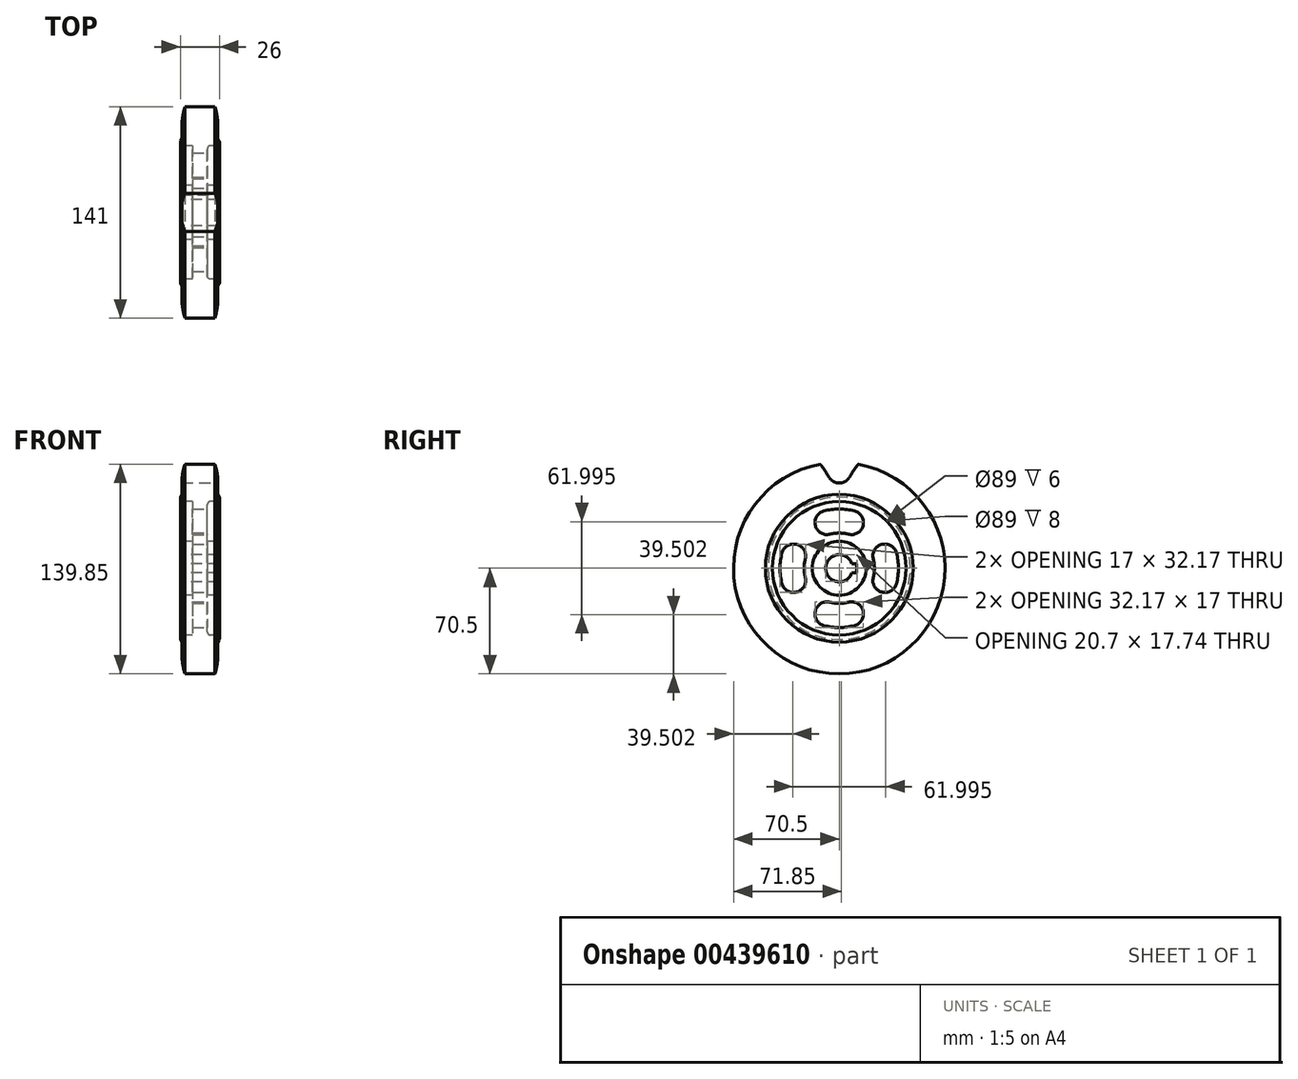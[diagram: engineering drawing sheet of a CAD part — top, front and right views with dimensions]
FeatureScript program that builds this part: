
annotation { "Feature Type Name" : "Feature", "Feature Type Description" : "" }
export const myFeature = defineFeature(function(context is Context, id is Id, definition is map)
    precondition{}
    {
        {
            var Q0;
            Q0=qCreatedBy(makeId("Front.planeOp"),FACE);
            var sketch = newSketch(context, id + "F0", { "sketchPlane" : qUnion([Q0])});
            skLineSegment(sketch, "E0", {"start": v(-89.89, 0) * mm, "end": v(89.89, 0) * mm, "construction": true});
            skLineSegment(sketch, "E1", {"start": v(0, -64.7) * mm, "end": v(0, 108.64) * mm, "construction": true});
            skLineSegment(sketch, "E2", {"start": v(0, 9) * mm, "end": v(-13, 9) * mm});
            skLineSegment(sketch, "E3", {"start": v(-13, 9) * mm, "end": v(-13, 44.5) * mm});
            skLineSegment(sketch, "E4", {"start": v(-13, 44.5) * mm, "end": v(-13, 47.5) * mm});
            skArc(sketch, "E5", {"start": v(-12, 57.23) * mm, "mid": v(-11.5, 63.94) * mm, "end": v(-10, 70.5) * mm});
            skLineSegment(sketch, "E6", {"start": v(-10, 70.5) * mm, "end": v(0, 70.5) * mm});
            skLineSegment(sketch, "E7.MirrorCS", {"start": v(13, 44.5) * mm, "end": v(13, 47.5) * mm});
            skLineSegment(sketch, "E8.MirrorCS", {"start": v(13, 9) * mm, "end": v(13, 44.5) * mm});
            skLineSegment(sketch, "E9.MirrorCS", {"start": v(0, 9) * mm, "end": v(13, 9) * mm});
            skLineSegment(sketch, "E10.bottom", {"start": v(-16.55, 44.5) * mm, "end": v(-5, 44.5) * mm});
            skLineSegment(sketch, "E10.top", {"start": v(-16.55, 18) * mm, "end": v(-5, 18) * mm});
            skLineSegment(sketch, "E10.left", {"start": v(-16.55, 44.5) * mm, "end": v(-16.55, 18) * mm});
            skLineSegment(sketch, "E10.right", {"start": v(-5, 44.5) * mm, "end": v(-5, 18) * mm});
            skLineSegment(sketch, "E11.MirrorCS", {"start": v(5, 44.5) * mm, "end": v(5, 18) * mm});
            skLineSegment(sketch, "E12.MirrorCS", {"start": v(16.55, 44.5) * mm, "end": v(5, 44.5) * mm});
            skLineSegment(sketch, "E13.MirrorCS", {"start": v(16.55, 18) * mm, "end": v(5, 18) * mm});
            skLineSegment(sketch, "E14.MirrorCS", {"start": v(16.55, 44.5) * mm, "end": v(16.55, 18) * mm});
            skLineSegment(sketch, "E15", {"start": v(-13, 47.5) * mm, "end": v(-12, 49.25) * mm});
            skLineSegment(sketch, "E16", {"start": v(-12, 49.25) * mm, "end": v(-12, 57.23) * mm});
            skArc(sketch, "E17.MirrorCS", {"start": v(12, 57.23) * mm, "mid": v(11.5, 63.94) * mm, "end": v(10, 70.5) * mm});
            skLineSegment(sketch, "E18.MirrorCS", {"start": v(12, 49.25) * mm, "end": v(12, 57.23) * mm});
            skLineSegment(sketch, "E19.MirrorCS", {"start": v(13, 47.5) * mm, "end": v(12, 49.25) * mm});
            skLineSegment(sketch, "E20.MirrorCS", {"start": v(0, 205.7) * mm, "end": v(0, 32.36) * mm, "construction": true});
            skLineSegment(sketch, "E21.MirrorCS", {"start": v(10, 70.5) * mm, "end": v(0, 70.5) * mm});
            skSolve(sketch);
        }
        {
            var Q0;
            {var subQ1=sQuery(id+"F0.wireOp",EDGE,"E2");Q0=makeQuery(id+"F0.imprint","IMPRINT",FACE,{"disambiguationData":[TD([[makeQuery(id+"F0.imprint","IMPRINT",EDGE,{"derivedFrom":subQ1}),-1.0]])]});}
            var Q1;
            Q1=sQuery(id+"F0.wireOp",EDGE,"E0");
            revolve(context, id + "F1", {"entities" : qUnion([Q0]), "axis" : qUnion([Q1]), "revolveType" : RevolveType.FULL});
        }
        {
            var Q0;
            Q0=qCreatedBy(makeId("Right.planeOp"),FACE);
            var sketch = newSketch(context, id + "F2", { "sketchPlane" : qUnion([Q0])});
            skLineSegment(sketch, "E22", {"start": v(0, 74.56) * mm, "end": v(0, -73.36) * mm, "construction": true});
            skCircle(sketch, "E23", {"center": v(0, 0) * mm, "radius": 64.75 * mm, "construction": true});
            skLineSegment(sketch, "E24", {"start": v(0, 64.75) * mm, "end": v(84.25, 16.1) * mm, "construction": true});
            skLineSegment(sketch, "E25", {"start": v(0, 64.75) * mm, "end": v(-84.25, 16.1) * mm, "construction": true});
            skArc(sketch, "E26", {"start": v(-6.87, 60.78) * mm, "mid": v(0, 56.81) * mm, "end": v(6.87, 60.78) * mm});
            skArc(sketch, "E27", {"start": v(11.86, 68.34) * mm, "mid": v(9.25, 64.64) * mm, "end": v(6.87, 60.78) * mm});
            skArc(sketch, "E28", {"start": v(11.86, 68.34) * mm, "mid": v(12.27, 68.86) * mm, "end": v(12.7, 69.35) * mm});
            skArc(sketch, "E29.MirrorCS", {"start": v(-11.86, 68.34) * mm, "mid": v(-12.27, 68.86) * mm, "end": v(-12.7, 69.35) * mm});
            skArc(sketch, "E30.MirrorCS", {"start": v(-11.86, 68.34) * mm, "mid": v(-9.25, 64.64) * mm, "end": v(-6.87, 60.78) * mm});
            skPoint(sketch, "E31.orphan", {"position": v(21.73, 73.23) * mm});
            skPoint(sketch, "E32.orphan", {"position": v(-21.73, 73.23) * mm});
            skArc(sketch, "E33.trimOffspring", {"start": v(12.7, 69.35) * mm, "mid": v(0, 70.5) * mm, "end": v(-12.7, 69.35) * mm});
            skSolve(sketch);
        }
        {
            var Q0;
            Q0=makeQuery(id+"F2.imprint","IMPRINT",FACE,{"disambiguationData":[TD([[makeQuery(id+"F2.imprint","IMPRINT",EDGE,{"derivedFrom":sQuery(id+"F2.wireOp",EDGE,"E26")}),1.0]])]});
            extrude(context, id + "F3", {"entities" : qUnion([Q0]), "operationType" : NewBodyOperationType.REMOVE, "endBound" : BoundingType.THROUGH_ALL, "oppositeDirection" : true, "depth" : 25 * mm, "hasSecondDirection" : true, "secondDirectionBound" : BoundingType.THROUGH_ALL, "secondDirectionOppositeDirection" : false, "secondDirectionDepth" : 25 * mm});
        }
        {
            var Q0;
            Q0=qCreatedBy(makeId("Right.planeOp"),FACE);
            var sketch = newSketch(context, id + "F4", { "sketchPlane" : qUnion([Q0])});
            skLineSegment(sketch, "E34", {"start": v(0, -69.16) * mm, "end": v(0, 68.82) * mm, "construction": true});
            skLineSegment(sketch, "E35", {"start": v(-70.48, 0) * mm, "end": v(76.97, 0) * mm, "construction": true});
            skLineSegment(sketch, "E36.bottom", {"start": v(4.41, 3) * mm, "end": v(11.7, 3) * mm});
            skLineSegment(sketch, "E36.top", {"start": v(4.41, -3) * mm, "end": v(11.7, -3) * mm});
            skLineSegment(sketch, "E36.left", {"start": v(4.41, 3) * mm, "end": v(4.41, -3) * mm});
            skLineSegment(sketch, "E36.right", {"start": v(11.7, 3) * mm, "end": v(11.7, -3) * mm});
            skLineSegment(sketch, "E37", {"start": v(-9, 11.79) * mm, "end": v(-9, -13.84) * mm, "construction": true});
            skCircle(sketch, "E38", {"center": v(0, 0) * mm, "radius": 31.5 * mm, "construction": true});
            skLineSegment(sketch, "E39", {"start": v(0, 0) * mm, "end": v(-40.07, 10.74) * mm, "construction": true});
            skLineSegment(sketch, "E40", {"start": v(0, 0) * mm, "end": v(-40.07, -10.74) * mm, "construction": true});
            skArc(sketch, "E41", {"start": v(-22.7, 6.08) * mm, "mid": v(-28.36, 15.88) * mm, "end": v(-38.15, 10.22) * mm});
            skArc(sketch, "E42", {"start": v(-38.15, -10.22) * mm, "mid": v(-28.36, -15.88) * mm, "end": v(-22.7, -6.08) * mm});
            skArc(sketch, "E43", {"start": v(-38.15, 10.22) * mm, "mid": v(-39.5, 0) * mm, "end": v(-38.15, -10.22) * mm});
            skArc(sketch, "E44", {"start": v(-22.7, 6.08) * mm, "mid": v(-23.5, 0) * mm, "end": v(-22.7, -6.08) * mm});
            skArc(sketch, "E45.1.0", {"start": v(-6.08, -22.7) * mm, "mid": v(-15.88, -28.36) * mm, "end": v(-10.22, -38.15) * mm});
            skArc(sketch, "E45.1.1", {"start": v(-10.22, -38.15) * mm, "mid": v(0, -39.5) * mm, "end": v(10.22, -38.15) * mm});
            skArc(sketch, "E45.1.2", {"start": v(-6.08, -22.7) * mm, "mid": v(0, -23.5) * mm, "end": v(6.08, -22.7) * mm});
            skArc(sketch, "E45.1.3", {"start": v(10.22, -38.15) * mm, "mid": v(15.88, -28.36) * mm, "end": v(6.08, -22.7) * mm});
            skArc(sketch, "E45.2.0", {"start": v(22.7, -6.08) * mm, "mid": v(28.36, -15.88) * mm, "end": v(38.15, -10.22) * mm});
            skArc(sketch, "E45.2.1", {"start": v(38.15, -10.22) * mm, "mid": v(39.5, 0) * mm, "end": v(38.15, 10.22) * mm});
            skArc(sketch, "E45.2.2", {"start": v(22.7, -6.08) * mm, "mid": v(23.5, 0) * mm, "end": v(22.7, 6.08) * mm});
            skArc(sketch, "E45.2.3", {"start": v(38.15, 10.22) * mm, "mid": v(28.36, 15.88) * mm, "end": v(22.7, 6.08) * mm});
            skArc(sketch, "E45.3.0", {"start": v(6.08, 22.7) * mm, "mid": v(15.88, 28.36) * mm, "end": v(10.22, 38.15) * mm});
            skArc(sketch, "E45.3.1", {"start": v(10.22, 38.15) * mm, "mid": v(0, 39.5) * mm, "end": v(-10.22, 38.15) * mm});
            skArc(sketch, "E45.3.2", {"start": v(6.08, 22.7) * mm, "mid": v(0, 23.5) * mm, "end": v(-6.08, 22.7) * mm});
            skArc(sketch, "E45.3.3", {"start": v(-10.22, 38.15) * mm, "mid": v(-15.88, 28.36) * mm, "end": v(-6.08, 22.7) * mm});
            skSolve(sketch);
        }
        {
            var Q0;
            Q0 = qSketchRegion(id + "F4", true);
            extrude(context, id + "F5", {"entities" : qUnion([Q0]), "operationType" : NewBodyOperationType.REMOVE, "endBound" : BoundingType.THROUGH_ALL, "oppositeDirection" : true, "depth" : 50 * mm, "hasSecondDirection" : true, "secondDirectionBound" : BoundingType.THROUGH_ALL, "secondDirectionOppositeDirection" : false, "secondDirectionDepth" : 25 * mm});
        }
        {
            var Q0;
            Q0=makeQuery(id+"F1.opRevolve","SWEPT_EDGE",EDGE,{"disambiguationData":[OSD([sQuery(id+"F0.wireOp",EDGE,"E11.MirrorCS"),sQuery(id+"F0.wireOp",EDGE,"E12.MirrorCS")])]});
            var Q1;
            Q1=makeQuery(id+"F1.opRevolve","SWEPT_EDGE",EDGE,{"disambiguationData":[OSD([sQuery(id+"F0.wireOp",EDGE,"3cedc181-8574-4f3b-a421-16c1fa0b98120.MirrorCS"),sQuery(id+"F0.wireOp",EDGE,"E7.MirrorCS")])]});
            fillet(context, id + "F6", {"entities" : qUnion([Q0, Q1]), "radius" : 2 * mm, "tangentPropagation" : true, "allowEdgeOverflow" : false});
        }
    });
